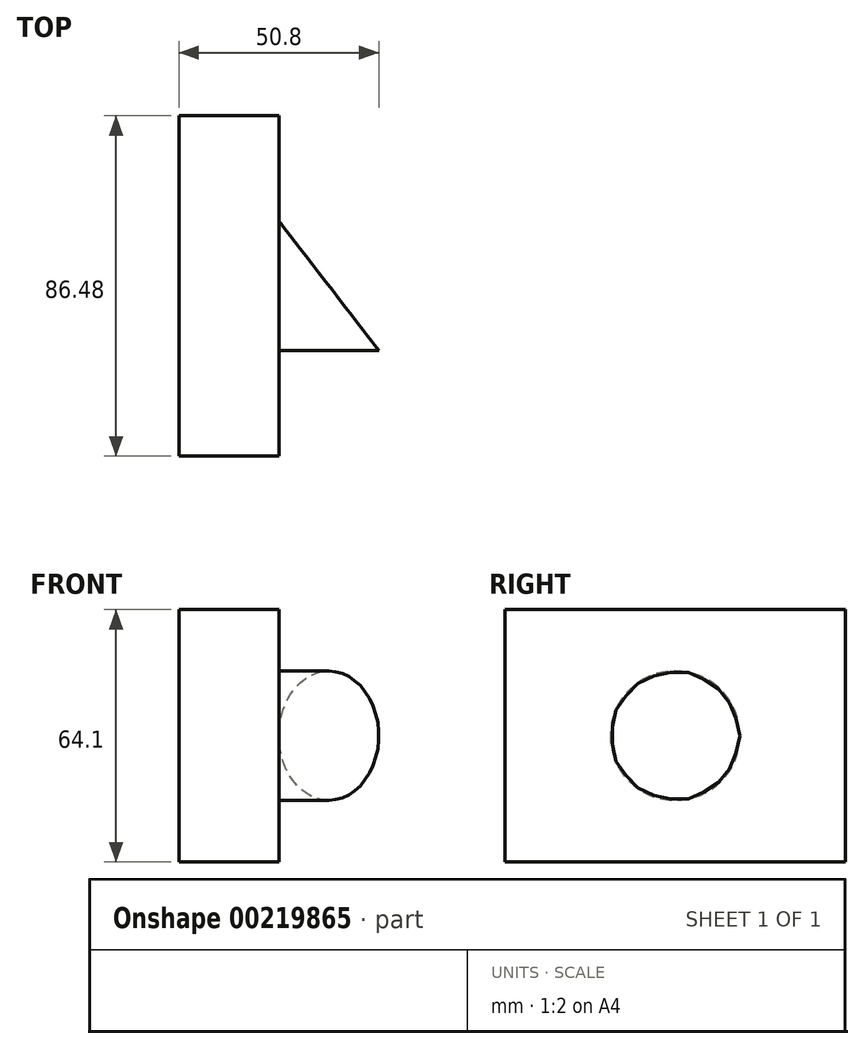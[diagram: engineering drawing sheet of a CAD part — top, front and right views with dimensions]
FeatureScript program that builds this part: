
annotation { "Feature Type Name" : "Feature", "Feature Type Description" : "" }
export const myFeature = defineFeature(function(context is Context, id is Id, definition is map)
    precondition{}
    {
        {
            var Q0;
            Q0=qCreatedBy(makeId("Right.planeOp"),FACE);
            var sketch = newSketch(context, id + "F0", { "sketchPlane" : qUnion([Q0])});
            skLineSegment(sketch, "E0.bottom", {"start": v(43.24, 32.05) * mm, "end": v(-43.24, 32.05) * mm});
            skLineSegment(sketch, "E0.top", {"start": v(43.24, -32.05) * mm, "end": v(-43.24, -32.05) * mm});
            skLineSegment(sketch, "E0.left", {"start": v(43.24, 32.05) * mm, "end": v(43.24, -32.05) * mm});
            skLineSegment(sketch, "E0.right", {"start": v(-43.24, 32.05) * mm, "end": v(-43.24, -32.05) * mm});
            skPoint(sketch, "E0.middle", {"position": v(0, 0) * mm});
            skSolve(sketch);
        }
        {
            var Q0;
            Q0=makeQuery(id+"F0.imprint","IMPRINT",FACE,{"disambiguationData":[TD([[makeQuery(id+"F0.imprint","IMPRINT",EDGE,{"derivedFrom":sQuery(id+"F0.wireOp",EDGE,"E0.bottom")}),1.0]])]});
            extrude(context, id + "F1", {"entities" : qUnion([Q0]), "depth" : 25.4 * mm});
        }
        {
            var Q0;
            Q0=makeQuery(id+"F1.opExtrude","CAP_FACE",FACE,{"disambiguationData":[OSD([sQuery(id+"F0.wireOp",EDGE,"E0.bottom"),sQuery(id+"F0.wireOp",EDGE,"E0.top"),sQuery(id+"F0.wireOp",EDGE,"E0.left"),sQuery(id+"F0.wireOp",EDGE,"E0.right")])],"isStart":false});
            var sketch = newSketch(context, id + "F2", { "sketchPlane" : qUnion([Q0])});
            skCircle(sketch, "E1", {"center": v(0, 0) * mm, "radius": 16.45 * mm});
            skSolve(sketch);
        }
        {
            var Q0;
            Q0=makeQuery(id+"F2.imprint","IMPRINT",FACE,{"disambiguationData":[TD([[makeQuery(id+"F2.imprint","IMPRINT",EDGE,{"derivedFrom":sQuery(id+"F2.wireOp",EDGE,"E1")}),1.0]])]});
            extrude(context, id + "F3", {"entities" : qUnion([Q0]), "operationType" : NewBodyOperationType.ADD, "depth" : 25.4 * mm});
        }
        {
            var Q0;
            Q0=makeQuery(id+"F1.opExtrude","SWEPT_FACE",FACE,{"disambiguationData":[OSD([sQuery(id+"F0.wireOp",EDGE,"E0.top")])]});
            var sketch = newSketch(context, id + "F4", { "sketchPlane" : qUnion([Q0])});
            skLineSegment(sketch, "E2.0", {"start": v(50.8, 16.45) * mm, "end": v(50.8, -16.45) * mm});
            skLineSegment(sketch, "E3", {"start": v(50.8, -16.45) * mm, "end": v(25.4, -16.45) * mm});
            skLineSegment(sketch, "E4", {"start": v(25.4, -16.45) * mm, "end": v(50.8, 16.45) * mm});
            skSolve(sketch);
        }
        {
            var Q0;
            Q0 = qSketchRegion(id + "F4", true);
            extrude(context, id + "F5", {"entities" : qUnion([Q0]), "operationType" : NewBodyOperationType.REMOVE, "endBound" : BoundingType.THROUGH_ALL, "oppositeDirection" : true, "depth" : 25.4 * mm});
        }
    });
